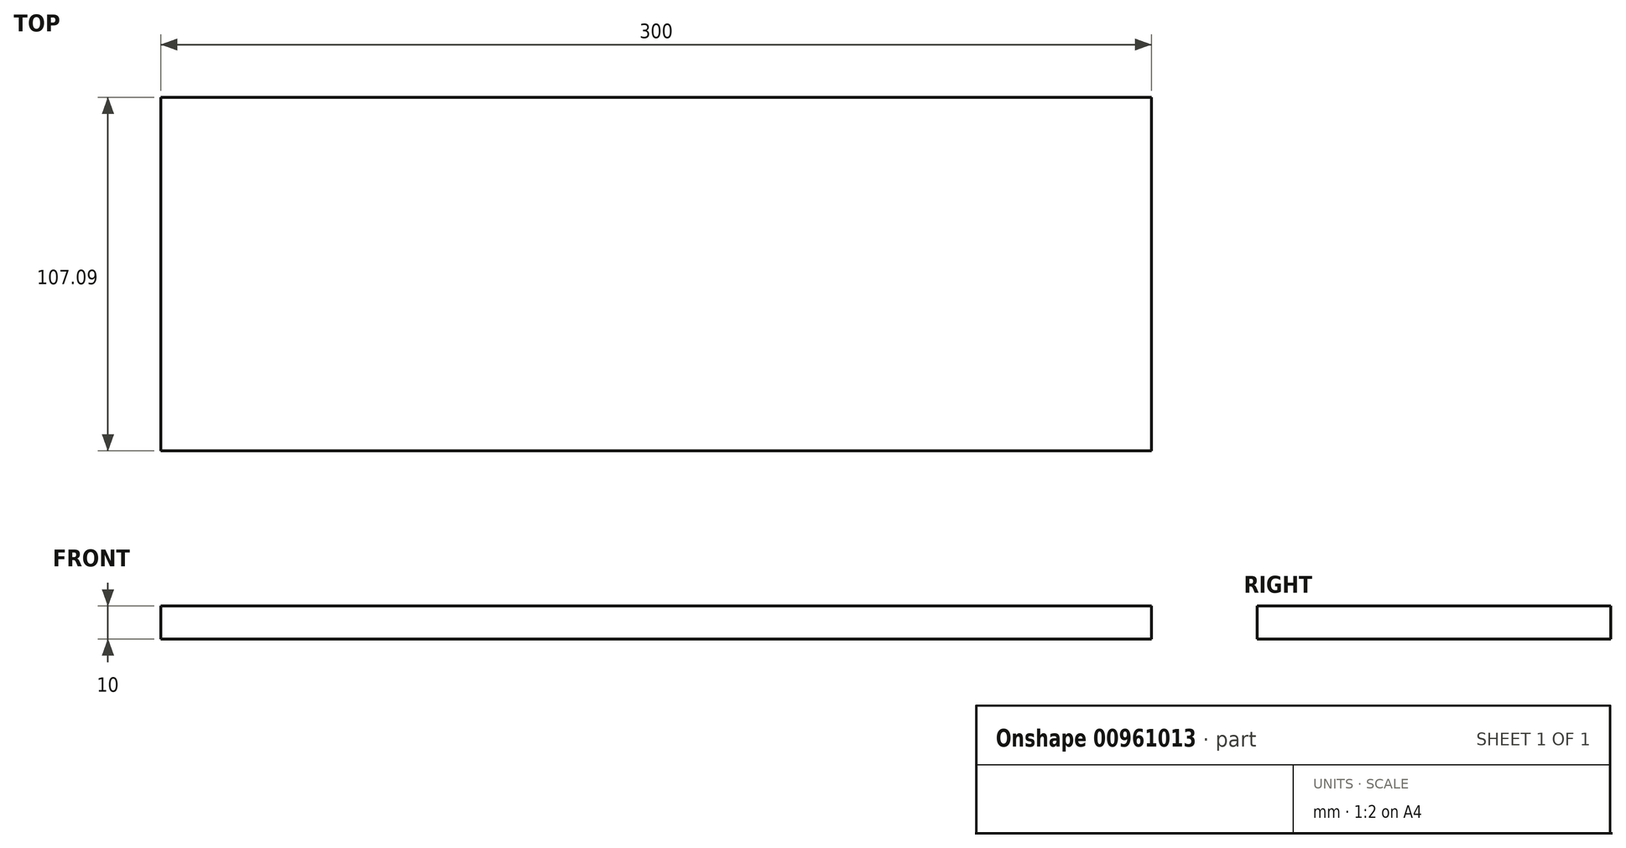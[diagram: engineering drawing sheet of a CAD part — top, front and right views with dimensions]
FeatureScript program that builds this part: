
annotation { "Feature Type Name" : "Feature", "Feature Type Description" : "" }
export const myFeature = defineFeature(function(context is Context, id is Id, definition is map)
    precondition{}
    {
        {
            var Q0;
            Q0=qCreatedBy(makeId("Top.planeOp"),FACE);
            var sketch = newSketch(context, id + "F0", { "sketchPlane" : qUnion([Q0])});
            skLineSegment(sketch, "E0.bottom", {"start": v(-145.73, -56.37) * mm, "end": v(154.27, -56.37) * mm});
            skLineSegment(sketch, "E0.top", {"start": v(-145.73, 50.72) * mm, "end": v(154.27, 50.72) * mm});
            skLineSegment(sketch, "E0.left", {"start": v(-145.73, -56.37) * mm, "end": v(-145.73, 50.72) * mm});
            skLineSegment(sketch, "E0.right", {"start": v(154.27, -56.37) * mm, "end": v(154.27, 50.72) * mm});
            skSolve(sketch);
        }
        {
            var Q0;
            Q0 = qSketchRegion(id + "F0", true);
            extrude(context, id + "F1", {"entities" : qUnion([Q0]), "depth" : 10 * mm, "offsetDistance" : 25.4 * mm});
        }
    });
